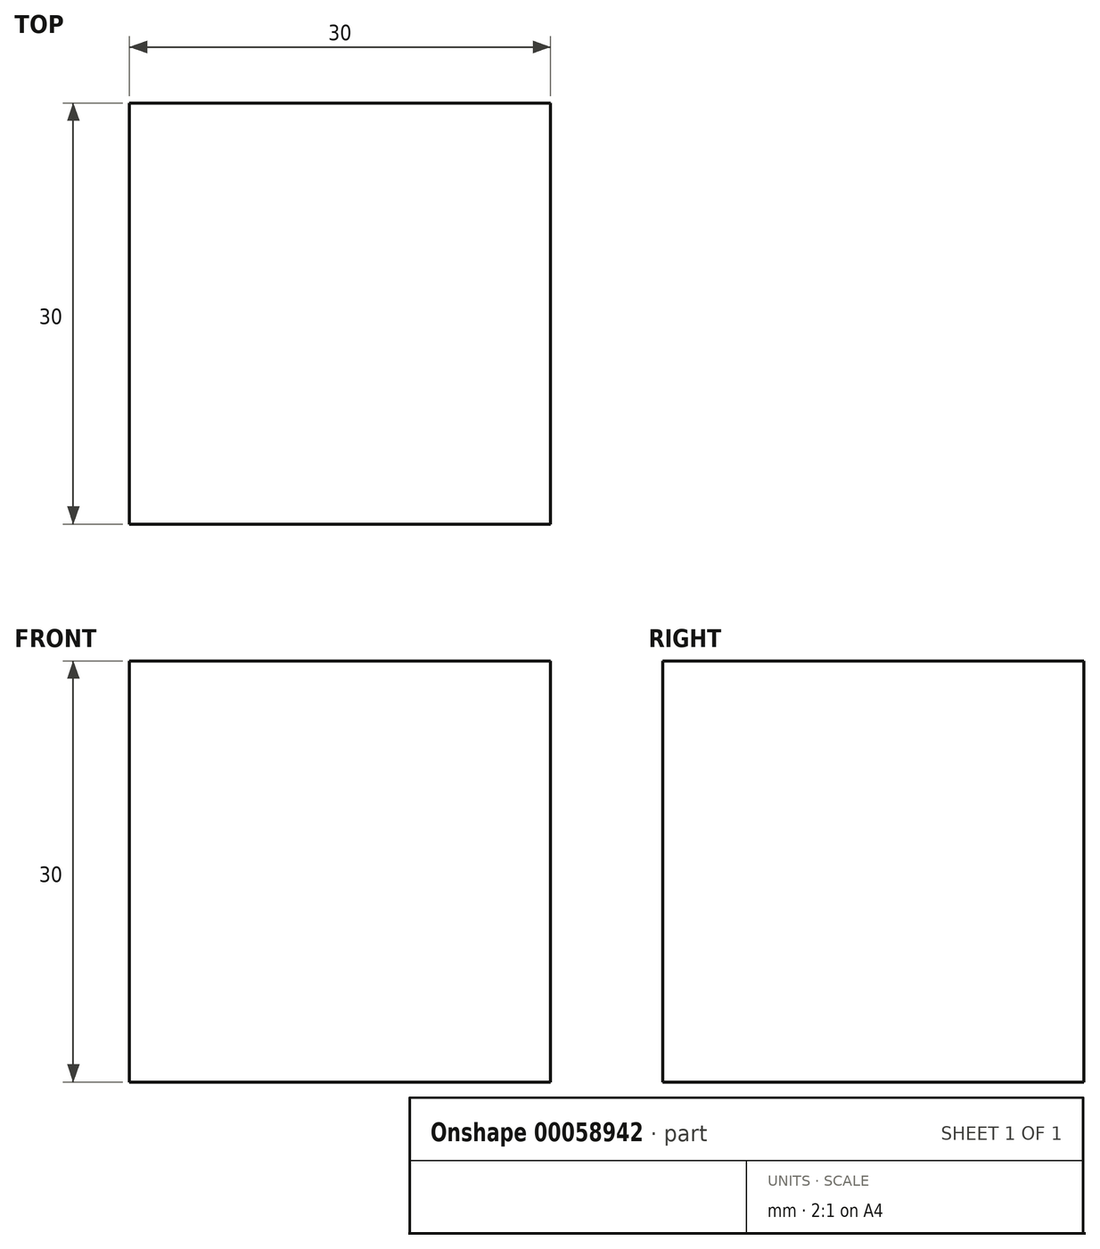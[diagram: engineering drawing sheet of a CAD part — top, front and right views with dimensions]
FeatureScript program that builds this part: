
annotation { "Feature Type Name" : "Feature", "Feature Type Description" : "" }
export const myFeature = defineFeature(function(context is Context, id is Id, definition is map)
    precondition{}
    {
        {
            var Q0;
            Q0=qCreatedBy(makeId("Front.planeOp"),FACE);
            var sketch = newSketch(context, id + "F0", { "sketchPlane" : qUnion([Q0])});
            skLineSegment(sketch, "E0.bottom", {"start": v(0, 0) * mm, "end": v(-30, 0) * mm});
            skLineSegment(sketch, "E0.top", {"start": v(0, 30) * mm, "end": v(-30, 30) * mm});
            skLineSegment(sketch, "E0.left", {"start": v(0, 0) * mm, "end": v(0, 30) * mm});
            skLineSegment(sketch, "E0.right", {"start": v(-30, 0) * mm, "end": v(-30, 30) * mm});
            skSolve(sketch);
        }
        {
            var Q0;
            Q0 = qSketchRegion(id + "F0", true);
            extrude(context, id + "F1", {"entities" : qUnion([Q0]), "depth" : 30 * mm});
        }
    });
